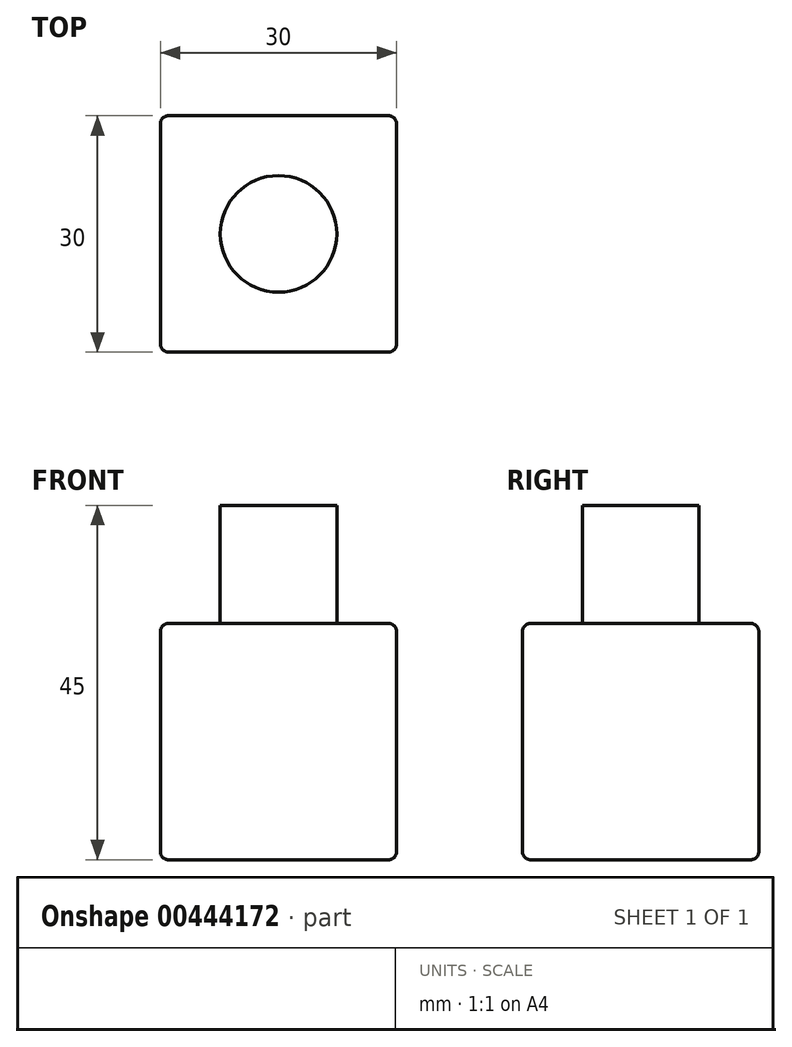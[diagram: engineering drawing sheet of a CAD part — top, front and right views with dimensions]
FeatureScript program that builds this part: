
annotation { "Feature Type Name" : "Feature", "Feature Type Description" : "" }
export const myFeature = defineFeature(function(context is Context, id is Id, definition is map)
    precondition{}
    {
        {
            var Q0;
            Q0=qCreatedBy(makeId("Top.planeOp"),FACE);
            var sketch = newSketch(context, id + "F0", { "sketchPlane" : qUnion([Q0])});
            skLineSegment(sketch, "E0.bottom", {"start": v(-13.03, -4.99) * mm, "end": v(16.97, -4.99) * mm});
            skLineSegment(sketch, "E0.top", {"start": v(-13.03, -34.99) * mm, "end": v(16.97, -34.99) * mm});
            skLineSegment(sketch, "E0.left", {"start": v(-13.03, -4.99) * mm, "end": v(-13.03, -34.99) * mm});
            skLineSegment(sketch, "E0.right", {"start": v(16.97, -4.99) * mm, "end": v(16.97, -34.99) * mm});
            skCircle(sketch, "E1", {"center": v(1.97, -19.99) * mm, "radius": 7.4 * mm});
            skSolve(sketch);
        }
        {
            var Q0;
            Q0=makeQuery(id+"F0.imprint","IMPRINT",FACE,{"disambiguationData":[TD([[makeQuery(id+"F0.imprint","IMPRINT",EDGE,{"derivedFrom":sQuery(id+"F0.wireOp",EDGE,"E1")}),1.0]])]});
            extrude(context, id + "F1", {"entities" : qUnion([Q0]), "depth" : 45 * mm});
        }
        {
            var Q0;
            Q0=makeQuery(id+"F0.imprint","IMPRINT",FACE,{"disambiguationData":[TD([[makeQuery(id+"F0.imprint","IMPRINT",EDGE,{"derivedFrom":sQuery(id+"F0.wireOp",EDGE,"E0.bottom")}),-1.0]])]});
            extrude(context, id + "F2", {"entities" : qUnion([Q0]), "operationType" : NewBodyOperationType.ADD, "depth" : 30 * mm});
        }
        {
            var Q0;
            Q0=makeQuery(id+"F2.opExtrude","SWEPT_FACE",FACE,{"disambiguationData":[OSD([sQuery(id+"F0.wireOp",EDGE,"E0.bottom")])]});
            var Q1;
            Q1=makeQuery(id+"F2.opExtrude","SWEPT_FACE",FACE,{"disambiguationData":[OSD([sQuery(id+"F0.wireOp",EDGE,"E0.left")])]});
            var Q2;
            Q2=makeQuery(id+"F2.opExtrude","SWEPT_FACE",FACE,{"disambiguationData":[OSD([sQuery(id+"F0.wireOp",EDGE,"E0.top")])]});
            var Q3;
            Q3=makeQuery(id+"F2.opExtrude","SWEPT_FACE",FACE,{"disambiguationData":[OSD([sQuery(id+"F0.wireOp",EDGE,"E0.right")])]});
            var Q4;
            {var subQ0=sQuery(id+"F0.wireOp",EDGE,"E1");Q4=makeQuery(id+"F2.boolean.opBoolean","MERGE",FACE,{"derivedFrom":[makeQuery(id+"F1.opExtrude","CAP_FACE",FACE,{"disambiguationData":[OSD([subQ0])],"isStart":true}),makeQuery(id+"F2.opExtrude","CAP_FACE",FACE,{"disambiguationData":[OSD([sQuery(id+"F0.wireOp",EDGE,"E0.bottom"),sQuery(id+"F0.wireOp",EDGE,"E0.top"),sQuery(id+"F0.wireOp",EDGE,"E0.left"),sQuery(id+"F0.wireOp",EDGE,"E0.right"),subQ0])],"isStart":true})]});}
            fillet(context, id + "F3", {"entities" : qUnion([Q0, Q1, Q2, Q3, Q4]), "radius" : 1 * mm, "tangentPropagation" : true, "allowEdgeOverflow" : false});
        }
    });
